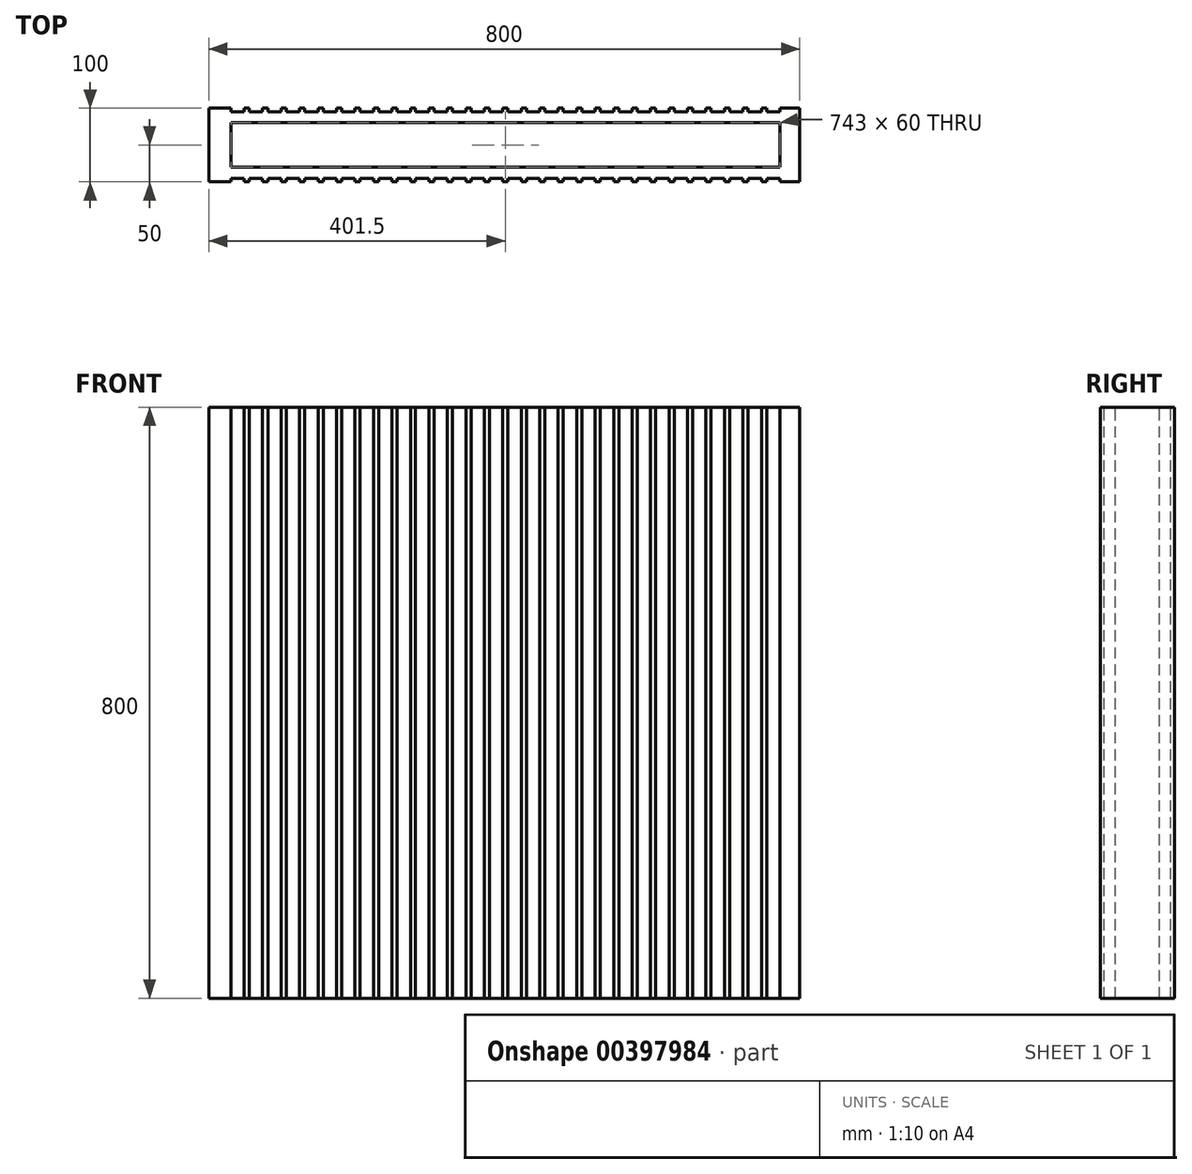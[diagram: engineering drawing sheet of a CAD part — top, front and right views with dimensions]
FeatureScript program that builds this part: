
annotation { "Feature Type Name" : "Feature", "Feature Type Description" : "" }
export const myFeature = defineFeature(function(context is Context, id is Id, definition is map)
    precondition{}
    {
        {
            var Q0;
            Q0=qCreatedBy(makeId("Top.planeOp"),FACE);
            var sketch = newSketch(context, id + "F0", { "sketchPlane" : qUnion([Q0])});
            skLineSegment(sketch, "E0.bottom", {"start": v(0, 0) * mm, "end": v(800, 0) * mm});
            skLineSegment(sketch, "E0.top", {"start": v(0, 100) * mm, "end": v(800, 100) * mm});
            skLineSegment(sketch, "E0.left", {"start": v(0, 0) * mm, "end": v(0, 100) * mm});
            skLineSegment(sketch, "E0.right", {"start": v(800, 0) * mm, "end": v(800, 100) * mm});
            skSolve(sketch);
        }
        {
            var Q0;
            Q0=makeQuery(id+"F0.imprint","IMPRINT",FACE,{"disambiguationData":[TD([[makeQuery(id+"F0.imprint","IMPRINT",EDGE,{"derivedFrom":sQuery(id+"F0.wireOp",EDGE,"E0.bottom")}),1.0]])]});
            extrude(context, id + "F1", {"entities" : qUnion([Q0]), "depth" : 800 * mm, "offsetDistance" : 25 * mm});
        }
        {
            var Q0;
            Q0=makeQuery(id+"F1.opExtrude","CAP_FACE",FACE,{"disambiguationData":[OSD([sQuery(id+"F0.wireOp",EDGE,"E0.bottom"),sQuery(id+"F0.wireOp",EDGE,"E0.top"),sQuery(id+"F0.wireOp",EDGE,"E0.left"),sQuery(id+"F0.wireOp",EDGE,"E0.right")])],"isStart":false});
            var sketch = newSketch(context, id + "F2", { "sketchPlane" : qUnion([Q0])});
            skLineSegment(sketch, "E1.top", {"start": v(30, 20) * mm, "end": v(773, 20) * mm});
            skLineSegment(sketch, "E1.left", {"start": v(30, 50) * mm, "end": v(30, 20) * mm});
            skLineSegment(sketch, "E1.right", {"start": v(773, 50) * mm, "end": v(773, 20) * mm});
            skLineSegment(sketch, "E2.bottom", {"start": v(30, 0) * mm, "end": v(48, 0) * mm});
            skLineSegment(sketch, "E2.top", {"start": v(30, 5) * mm, "end": v(48, 5) * mm});
            skLineSegment(sketch, "E2.left", {"start": v(30, 0) * mm, "end": v(30, 5) * mm});
            skLineSegment(sketch, "E2.right", {"start": v(48, 0) * mm, "end": v(48, 5) * mm});
            skLineSegment(sketch, "E3", {"start": v(0, 50) * mm, "end": v(975.65, 50) * mm, "construction": true});
            skLineSegment(sketch, "E4.1.0.0", {"start": v(55, 0) * mm, "end": v(73, 0) * mm});
            skLineSegment(sketch, "E4.1.0.1", {"start": v(55, 5) * mm, "end": v(73, 5) * mm});
            skLineSegment(sketch, "E4.1.0.2", {"start": v(73, 0) * mm, "end": v(73, 5) * mm});
            skLineSegment(sketch, "E4.1.0.3", {"start": v(55, 0) * mm, "end": v(55, 5) * mm});
            skLineSegment(sketch, "E4.2.0.0", {"start": v(80, 0) * mm, "end": v(98, 0) * mm});
            skLineSegment(sketch, "E4.2.0.1", {"start": v(80, 5) * mm, "end": v(98, 5) * mm});
            skLineSegment(sketch, "E4.2.0.2", {"start": v(98, 0) * mm, "end": v(98, 5) * mm});
            skLineSegment(sketch, "E4.2.0.3", {"start": v(80, 0) * mm, "end": v(80, 5) * mm});
            skLineSegment(sketch, "E4.3.0.0", {"start": v(105, 0) * mm, "end": v(123, 0) * mm});
            skLineSegment(sketch, "E4.3.0.1", {"start": v(105, 5) * mm, "end": v(123, 5) * mm});
            skLineSegment(sketch, "E4.3.0.2", {"start": v(123, 0) * mm, "end": v(123, 5) * mm});
            skLineSegment(sketch, "E4.3.0.3", {"start": v(105, 0) * mm, "end": v(105, 5) * mm});
            skLineSegment(sketch, "E4.4.0.0", {"start": v(130, 0) * mm, "end": v(148, 0) * mm});
            skLineSegment(sketch, "E4.4.0.1", {"start": v(130, 5) * mm, "end": v(148, 5) * mm});
            skLineSegment(sketch, "E4.4.0.2", {"start": v(148, 0) * mm, "end": v(148, 5) * mm});
            skLineSegment(sketch, "E4.4.0.3", {"start": v(130, 0) * mm, "end": v(130, 5) * mm});
            skLineSegment(sketch, "E4.5.0.0", {"start": v(155, 0) * mm, "end": v(173, 0) * mm});
            skLineSegment(sketch, "E4.5.0.1", {"start": v(155, 5) * mm, "end": v(173, 5) * mm});
            skLineSegment(sketch, "E4.5.0.2", {"start": v(173, 0) * mm, "end": v(173, 5) * mm});
            skLineSegment(sketch, "E4.5.0.3", {"start": v(155, 0) * mm, "end": v(155, 5) * mm});
            skLineSegment(sketch, "E4.6.0.0", {"start": v(180, 0) * mm, "end": v(198, 0) * mm});
            skLineSegment(sketch, "E4.6.0.1", {"start": v(180, 5) * mm, "end": v(198, 5) * mm});
            skLineSegment(sketch, "E4.6.0.2", {"start": v(198, 0) * mm, "end": v(198, 5) * mm});
            skLineSegment(sketch, "E4.6.0.3", {"start": v(180, 0) * mm, "end": v(180, 5) * mm});
            skLineSegment(sketch, "E4.7.0.0", {"start": v(205, 0) * mm, "end": v(223, 0) * mm});
            skLineSegment(sketch, "E4.7.0.1", {"start": v(205, 5) * mm, "end": v(223, 5) * mm});
            skLineSegment(sketch, "E4.7.0.2", {"start": v(223, 0) * mm, "end": v(223, 5) * mm});
            skLineSegment(sketch, "E4.7.0.3", {"start": v(205, 0) * mm, "end": v(205, 5) * mm});
            skLineSegment(sketch, "E4.8.0.0", {"start": v(230, 0) * mm, "end": v(248, 0) * mm});
            skLineSegment(sketch, "E4.8.0.1", {"start": v(230, 5) * mm, "end": v(248, 5) * mm});
            skLineSegment(sketch, "E4.8.0.2", {"start": v(248, 0) * mm, "end": v(248, 5) * mm});
            skLineSegment(sketch, "E4.8.0.3", {"start": v(230, 0) * mm, "end": v(230, 5) * mm});
            skLineSegment(sketch, "E4.9.0.0", {"start": v(255, 0) * mm, "end": v(273, 0) * mm});
            skLineSegment(sketch, "E4.9.0.1", {"start": v(255, 5) * mm, "end": v(273, 5) * mm});
            skLineSegment(sketch, "E4.9.0.2", {"start": v(273, 0) * mm, "end": v(273, 5) * mm});
            skLineSegment(sketch, "E4.9.0.3", {"start": v(255, 0) * mm, "end": v(255, 5) * mm});
            skLineSegment(sketch, "E4.10.0.0", {"start": v(280, 0) * mm, "end": v(298, 0) * mm});
            skLineSegment(sketch, "E4.10.0.1", {"start": v(280, 5) * mm, "end": v(298, 5) * mm});
            skLineSegment(sketch, "E4.10.0.2", {"start": v(298, 0) * mm, "end": v(298, 5) * mm});
            skLineSegment(sketch, "E4.10.0.3", {"start": v(280, 0) * mm, "end": v(280, 5) * mm});
            skLineSegment(sketch, "E4.11.0.0", {"start": v(305, 0) * mm, "end": v(323, 0) * mm});
            skLineSegment(sketch, "E4.11.0.1", {"start": v(305, 5) * mm, "end": v(323, 5) * mm});
            skLineSegment(sketch, "E4.11.0.2", {"start": v(323, 0) * mm, "end": v(323, 5) * mm});
            skLineSegment(sketch, "E4.11.0.3", {"start": v(305, 0) * mm, "end": v(305, 5) * mm});
            skLineSegment(sketch, "E4.12.0.0", {"start": v(330, 0) * mm, "end": v(348, 0) * mm});
            skLineSegment(sketch, "E4.12.0.1", {"start": v(330, 5) * mm, "end": v(348, 5) * mm});
            skLineSegment(sketch, "E4.12.0.2", {"start": v(348, 0) * mm, "end": v(348, 5) * mm});
            skLineSegment(sketch, "E4.12.0.3", {"start": v(330, 0) * mm, "end": v(330, 5) * mm});
            skLineSegment(sketch, "E4.13.0.0", {"start": v(355, 0) * mm, "end": v(373, 0) * mm});
            skLineSegment(sketch, "E4.13.0.1", {"start": v(355, 5) * mm, "end": v(373, 5) * mm});
            skLineSegment(sketch, "E4.13.0.2", {"start": v(373, 0) * mm, "end": v(373, 5) * mm});
            skLineSegment(sketch, "E4.13.0.3", {"start": v(355, 0) * mm, "end": v(355, 5) * mm});
            skLineSegment(sketch, "E4.14.0.0", {"start": v(380, 0) * mm, "end": v(398, 0) * mm});
            skLineSegment(sketch, "E4.14.0.1", {"start": v(380, 5) * mm, "end": v(398, 5) * mm});
            skLineSegment(sketch, "E4.14.0.2", {"start": v(398, 0) * mm, "end": v(398, 5) * mm});
            skLineSegment(sketch, "E4.14.0.3", {"start": v(380, 0) * mm, "end": v(380, 5) * mm});
            skLineSegment(sketch, "E4.15.0.0", {"start": v(405, 0) * mm, "end": v(423, 0) * mm});
            skLineSegment(sketch, "E4.15.0.1", {"start": v(405, 5) * mm, "end": v(423, 5) * mm});
            skLineSegment(sketch, "E4.15.0.2", {"start": v(423, 0) * mm, "end": v(423, 5) * mm});
            skLineSegment(sketch, "E4.15.0.3", {"start": v(405, 0) * mm, "end": v(405, 5) * mm});
            skLineSegment(sketch, "E4.16.0.0", {"start": v(430, 0) * mm, "end": v(448, 0) * mm});
            skLineSegment(sketch, "E4.16.0.1", {"start": v(430, 5) * mm, "end": v(448, 5) * mm});
            skLineSegment(sketch, "E4.16.0.2", {"start": v(448, 0) * mm, "end": v(448, 5) * mm});
            skLineSegment(sketch, "E4.16.0.3", {"start": v(430, 0) * mm, "end": v(430, 5) * mm});
            skLineSegment(sketch, "E4.17.0.0", {"start": v(455, 0) * mm, "end": v(473, 0) * mm});
            skLineSegment(sketch, "E4.17.0.1", {"start": v(455, 5) * mm, "end": v(473, 5) * mm});
            skLineSegment(sketch, "E4.17.0.2", {"start": v(473, 0) * mm, "end": v(473, 5) * mm});
            skLineSegment(sketch, "E4.17.0.3", {"start": v(455, 0) * mm, "end": v(455, 5) * mm});
            skLineSegment(sketch, "E4.18.0.0", {"start": v(480, 0) * mm, "end": v(498, 0) * mm});
            skLineSegment(sketch, "E4.18.0.1", {"start": v(480, 5) * mm, "end": v(498, 5) * mm});
            skLineSegment(sketch, "E4.18.0.2", {"start": v(498, 0) * mm, "end": v(498, 5) * mm});
            skLineSegment(sketch, "E4.18.0.3", {"start": v(480, 0) * mm, "end": v(480, 5) * mm});
            skLineSegment(sketch, "E4.19.0.0", {"start": v(505, 0) * mm, "end": v(523, 0) * mm});
            skLineSegment(sketch, "E4.19.0.1", {"start": v(505, 5) * mm, "end": v(523, 5) * mm});
            skLineSegment(sketch, "E4.19.0.2", {"start": v(523, 0) * mm, "end": v(523, 5) * mm});
            skLineSegment(sketch, "E4.19.0.3", {"start": v(505, 0) * mm, "end": v(505, 5) * mm});
            skLineSegment(sketch, "E4.20.0.0", {"start": v(530, 0) * mm, "end": v(548, 0) * mm});
            skLineSegment(sketch, "E4.20.0.1", {"start": v(530, 5) * mm, "end": v(548, 5) * mm});
            skLineSegment(sketch, "E4.20.0.2", {"start": v(548, 0) * mm, "end": v(548, 5) * mm});
            skLineSegment(sketch, "E4.20.0.3", {"start": v(530, 0) * mm, "end": v(530, 5) * mm});
            skLineSegment(sketch, "E4.21.0.0", {"start": v(555, 0) * mm, "end": v(573, 0) * mm});
            skLineSegment(sketch, "E4.21.0.1", {"start": v(555, 5) * mm, "end": v(573, 5) * mm});
            skLineSegment(sketch, "E4.21.0.2", {"start": v(573, 0) * mm, "end": v(573, 5) * mm});
            skLineSegment(sketch, "E4.21.0.3", {"start": v(555, 0) * mm, "end": v(555, 5) * mm});
            skLineSegment(sketch, "E4.22.0.0", {"start": v(580, 0) * mm, "end": v(598, 0) * mm});
            skLineSegment(sketch, "E4.22.0.1", {"start": v(580, 5) * mm, "end": v(598, 5) * mm});
            skLineSegment(sketch, "E4.22.0.2", {"start": v(598, 0) * mm, "end": v(598, 5) * mm});
            skLineSegment(sketch, "E4.22.0.3", {"start": v(580, 0) * mm, "end": v(580, 5) * mm});
            skLineSegment(sketch, "E4.23.0.0", {"start": v(605, 0) * mm, "end": v(623, 0) * mm});
            skLineSegment(sketch, "E4.23.0.1", {"start": v(605, 5) * mm, "end": v(623, 5) * mm});
            skLineSegment(sketch, "E4.23.0.2", {"start": v(623, 0) * mm, "end": v(623, 5) * mm});
            skLineSegment(sketch, "E4.23.0.3", {"start": v(605, 0) * mm, "end": v(605, 5) * mm});
            skLineSegment(sketch, "E4.24.0.0", {"start": v(630, 0) * mm, "end": v(648, 0) * mm});
            skLineSegment(sketch, "E4.24.0.1", {"start": v(630, 5) * mm, "end": v(648, 5) * mm});
            skLineSegment(sketch, "E4.24.0.2", {"start": v(648, 0) * mm, "end": v(648, 5) * mm});
            skLineSegment(sketch, "E4.24.0.3", {"start": v(630, 0) * mm, "end": v(630, 5) * mm});
            skLineSegment(sketch, "E4.25.0.0", {"start": v(655, 0) * mm, "end": v(673, 0) * mm});
            skLineSegment(sketch, "E4.25.0.1", {"start": v(655, 5) * mm, "end": v(673, 5) * mm});
            skLineSegment(sketch, "E4.25.0.2", {"start": v(673, 0) * mm, "end": v(673, 5) * mm});
            skLineSegment(sketch, "E4.25.0.3", {"start": v(655, 0) * mm, "end": v(655, 5) * mm});
            skLineSegment(sketch, "E4.26.0.0", {"start": v(680, 0) * mm, "end": v(698, 0) * mm});
            skLineSegment(sketch, "E4.26.0.1", {"start": v(680, 5) * mm, "end": v(698, 5) * mm});
            skLineSegment(sketch, "E4.26.0.2", {"start": v(698, 0) * mm, "end": v(698, 5) * mm});
            skLineSegment(sketch, "E4.26.0.3", {"start": v(680, 0) * mm, "end": v(680, 5) * mm});
            skLineSegment(sketch, "E4.27.0.0", {"start": v(705, 0) * mm, "end": v(723, 0) * mm});
            skLineSegment(sketch, "E4.27.0.1", {"start": v(705, 5) * mm, "end": v(723, 5) * mm});
            skLineSegment(sketch, "E4.27.0.2", {"start": v(723, 0) * mm, "end": v(723, 5) * mm});
            skLineSegment(sketch, "E4.27.0.3", {"start": v(705, 0) * mm, "end": v(705, 5) * mm});
            skLineSegment(sketch, "E4.28.0.0", {"start": v(730, 0) * mm, "end": v(748, 0) * mm});
            skLineSegment(sketch, "E4.28.0.1", {"start": v(730, 5) * mm, "end": v(748, 5) * mm});
            skLineSegment(sketch, "E4.28.0.2", {"start": v(748, 0) * mm, "end": v(748, 5) * mm});
            skLineSegment(sketch, "E4.28.0.3", {"start": v(730, 0) * mm, "end": v(730, 5) * mm});
            skLineSegment(sketch, "E4.29.0.0", {"start": v(755, 0) * mm, "end": v(773, 0) * mm});
            skLineSegment(sketch, "E4.29.0.1", {"start": v(755, 5) * mm, "end": v(773, 5) * mm});
            skLineSegment(sketch, "E4.29.0.2", {"start": v(773, 0) * mm, "end": v(773, 5) * mm});
            skLineSegment(sketch, "E4.29.0.3", {"start": v(755, 0) * mm, "end": v(755, 5) * mm});
            skLineSegment(sketch, "E4.direction1", {"start": v(30, 0) * mm, "end": v(55, 0) * mm, "construction": true});
            skLineSegment(sketch, "E5.MirrorCS", {"start": v(673, 100) * mm, "end": v(673, 95) * mm});
            skLineSegment(sketch, "E6.MirrorCS", {"start": v(355, 100) * mm, "end": v(355, 95) * mm});
            skLineSegment(sketch, "E7.MirrorCS", {"start": v(255, 100) * mm, "end": v(255, 95) * mm});
            skLineSegment(sketch, "E8.MirrorCS", {"start": v(198, 100) * mm, "end": v(198, 95) * mm});
            skLineSegment(sketch, "E9.MirrorCS", {"start": v(680, 100) * mm, "end": v(680, 95) * mm});
            skLineSegment(sketch, "E10.MirrorCS", {"start": v(205, 100) * mm, "end": v(205, 95) * mm});
            skLineSegment(sketch, "E11.MirrorCS", {"start": v(348, 100) * mm, "end": v(348, 95) * mm});
            skLineSegment(sketch, "E12.MirrorCS", {"start": v(248, 100) * mm, "end": v(248, 95) * mm});
            skLineSegment(sketch, "E13.MirrorCS", {"start": v(30, 100) * mm, "end": v(48, 100) * mm});
            skLineSegment(sketch, "E14.MirrorCS", {"start": v(373, 100) * mm, "end": v(373, 95) * mm});
            skLineSegment(sketch, "E15.MirrorCS", {"start": v(273, 100) * mm, "end": v(273, 95) * mm});
            skLineSegment(sketch, "E16.MirrorCS", {"start": v(173, 100) * mm, "end": v(173, 95) * mm});
            skLineSegment(sketch, "E17.MirrorCS", {"start": v(573, 100) * mm, "end": v(573, 95) * mm});
            skLineSegment(sketch, "E18.MirrorCS", {"start": v(30, 100) * mm, "end": v(55, 100) * mm, "construction": true});
            skLineSegment(sketch, "E19.MirrorCS", {"start": v(455, 100) * mm, "end": v(455, 95) * mm});
            skLineSegment(sketch, "E20.MirrorCS", {"start": v(755, 100) * mm, "end": v(755, 95) * mm});
            skLineSegment(sketch, "E21.MirrorCS", {"start": v(655, 100) * mm, "end": v(655, 95) * mm});
            skLineSegment(sketch, "E22.MirrorCS", {"start": v(80, 100) * mm, "end": v(80, 95) * mm});
            skLineSegment(sketch, "E23.MirrorCS", {"start": v(30, 95) * mm, "end": v(48, 95) * mm});
            skLineSegment(sketch, "E24.MirrorCS", {"start": v(30, 100) * mm, "end": v(30, 95) * mm});
            skLineSegment(sketch, "E25.MirrorCS", {"start": v(48, 100) * mm, "end": v(48, 95) * mm});
            skLineSegment(sketch, "E26.MirrorCS", {"start": v(55, 100) * mm, "end": v(73, 100) * mm});
            skLineSegment(sketch, "E27.MirrorCS", {"start": v(55, 95) * mm, "end": v(73, 95) * mm});
            skLineSegment(sketch, "E28.MirrorCS", {"start": v(73, 100) * mm, "end": v(73, 95) * mm});
            skLineSegment(sketch, "E29.MirrorCS", {"start": v(55, 100) * mm, "end": v(55, 95) * mm});
            skLineSegment(sketch, "E30.MirrorCS", {"start": v(473, 100) * mm, "end": v(473, 95) * mm});
            skLineSegment(sketch, "E31.MirrorCS", {"start": v(773, 100) * mm, "end": v(773, 95) * mm});
            skLineSegment(sketch, "E32.MirrorCS", {"start": v(180, 100) * mm, "end": v(198, 100) * mm});
            skLineSegment(sketch, "E33.MirrorCS", {"start": v(580, 100) * mm, "end": v(598, 100) * mm});
            skLineSegment(sketch, "E34.MirrorCS", {"start": v(480, 100) * mm, "end": v(498, 100) * mm});
            skLineSegment(sketch, "E35.MirrorCS", {"start": v(380, 100) * mm, "end": v(398, 100) * mm});
            skLineSegment(sketch, "E36.MirrorCS", {"start": v(280, 100) * mm, "end": v(298, 100) * mm});
            skLineSegment(sketch, "E37.MirrorCS", {"start": v(680, 100) * mm, "end": v(698, 100) * mm});
            skLineSegment(sketch, "E38.MirrorCS", {"start": v(155, 100) * mm, "end": v(155, 95) * mm});
            skLineSegment(sketch, "E39.MirrorCS", {"start": v(555, 100) * mm, "end": v(555, 95) * mm});
            skLineSegment(sketch, "E40.MirrorCS", {"start": v(180, 95) * mm, "end": v(198, 95) * mm});
            skLineSegment(sketch, "E41.MirrorCS", {"start": v(580, 95) * mm, "end": v(598, 95) * mm});
            skLineSegment(sketch, "E42.MirrorCS", {"start": v(480, 95) * mm, "end": v(498, 95) * mm});
            skLineSegment(sketch, "E43.MirrorCS", {"start": v(380, 95) * mm, "end": v(398, 95) * mm});
            skLineSegment(sketch, "E44.MirrorCS", {"start": v(280, 95) * mm, "end": v(298, 95) * mm});
            skLineSegment(sketch, "E45.MirrorCS", {"start": v(680, 95) * mm, "end": v(698, 95) * mm});
            skLineSegment(sketch, "E46.MirrorCS", {"start": v(598, 100) * mm, "end": v(598, 95) * mm});
            skLineSegment(sketch, "E47.MirrorCS", {"start": v(498, 100) * mm, "end": v(498, 95) * mm});
            skLineSegment(sketch, "E48.MirrorCS", {"start": v(398, 100) * mm, "end": v(398, 95) * mm});
            skLineSegment(sketch, "E49.MirrorCS", {"start": v(298, 100) * mm, "end": v(298, 95) * mm});
            skLineSegment(sketch, "E50.MirrorCS", {"start": v(698, 100) * mm, "end": v(698, 95) * mm});
            skLineSegment(sketch, "E51.MirrorCS", {"start": v(580, 100) * mm, "end": v(580, 95) * mm});
            skLineSegment(sketch, "E52.MirrorCS", {"start": v(480, 100) * mm, "end": v(480, 95) * mm});
            skLineSegment(sketch, "E53.MirrorCS", {"start": v(380, 100) * mm, "end": v(380, 95) * mm});
            skLineSegment(sketch, "E54.MirrorCS", {"start": v(280, 100) * mm, "end": v(280, 95) * mm});
            skLineSegment(sketch, "E55.MirrorCS", {"start": v(180, 100) * mm, "end": v(180, 95) * mm});
            skLineSegment(sketch, "E56.MirrorCS", {"start": v(705, 100) * mm, "end": v(723, 100) * mm});
            skLineSegment(sketch, "E57.MirrorCS", {"start": v(205, 100) * mm, "end": v(223, 100) * mm});
            skLineSegment(sketch, "E58.MirrorCS", {"start": v(105, 100) * mm, "end": v(123, 100) * mm});
            skLineSegment(sketch, "E59.MirrorCS", {"start": v(605, 100) * mm, "end": v(623, 100) * mm});
            skLineSegment(sketch, "E60.MirrorCS", {"start": v(505, 100) * mm, "end": v(523, 100) * mm});
            skLineSegment(sketch, "E61.MirrorCS", {"start": v(405, 100) * mm, "end": v(423, 100) * mm});
            skLineSegment(sketch, "E62.MirrorCS", {"start": v(305, 100) * mm, "end": v(323, 100) * mm});
            skLineSegment(sketch, "E63.MirrorCS", {"start": v(205, 95) * mm, "end": v(223, 95) * mm});
            skLineSegment(sketch, "E64.MirrorCS", {"start": v(105, 95) * mm, "end": v(123, 95) * mm});
            skLineSegment(sketch, "E65.MirrorCS", {"start": v(605, 95) * mm, "end": v(623, 95) * mm});
            skLineSegment(sketch, "E66.MirrorCS", {"start": v(505, 95) * mm, "end": v(523, 95) * mm});
            skLineSegment(sketch, "E67.MirrorCS", {"start": v(405, 95) * mm, "end": v(423, 95) * mm});
            skLineSegment(sketch, "E68.MirrorCS", {"start": v(305, 95) * mm, "end": v(323, 95) * mm});
            skLineSegment(sketch, "E69.MirrorCS", {"start": v(705, 95) * mm, "end": v(723, 95) * mm});
            skLineSegment(sketch, "E70.MirrorCS", {"start": v(223, 100) * mm, "end": v(223, 95) * mm});
            skLineSegment(sketch, "E71.MirrorCS", {"start": v(123, 100) * mm, "end": v(123, 95) * mm});
            skLineSegment(sketch, "E72.MirrorCS", {"start": v(623, 100) * mm, "end": v(623, 95) * mm});
            skLineSegment(sketch, "E73.MirrorCS", {"start": v(523, 100) * mm, "end": v(523, 95) * mm});
            skLineSegment(sketch, "E74.MirrorCS", {"start": v(423, 100) * mm, "end": v(423, 95) * mm});
            skLineSegment(sketch, "E75.MirrorCS", {"start": v(323, 100) * mm, "end": v(323, 95) * mm});
            skLineSegment(sketch, "E76.MirrorCS", {"start": v(723, 100) * mm, "end": v(723, 95) * mm});
            skLineSegment(sketch, "E77.MirrorCS", {"start": v(105, 100) * mm, "end": v(105, 95) * mm});
            skLineSegment(sketch, "E78.MirrorCS", {"start": v(605, 100) * mm, "end": v(605, 95) * mm});
            skLineSegment(sketch, "E79.MirrorCS", {"start": v(505, 100) * mm, "end": v(505, 95) * mm});
            skLineSegment(sketch, "E80.MirrorCS", {"start": v(405, 100) * mm, "end": v(405, 95) * mm});
            skLineSegment(sketch, "E81.MirrorCS", {"start": v(305, 100) * mm, "end": v(305, 95) * mm});
            skLineSegment(sketch, "E82.MirrorCS", {"start": v(705, 100) * mm, "end": v(705, 95) * mm});
            skLineSegment(sketch, "E83.MirrorCS", {"start": v(230, 100) * mm, "end": v(248, 100) * mm});
            skLineSegment(sketch, "E84.MirrorCS", {"start": v(130, 100) * mm, "end": v(148, 100) * mm});
            skLineSegment(sketch, "E85.MirrorCS", {"start": v(630, 100) * mm, "end": v(648, 100) * mm});
            skLineSegment(sketch, "E86.MirrorCS", {"start": v(530, 100) * mm, "end": v(548, 100) * mm});
            skLineSegment(sketch, "E87.MirrorCS", {"start": v(430, 100) * mm, "end": v(448, 100) * mm});
            skLineSegment(sketch, "E88.MirrorCS", {"start": v(330, 100) * mm, "end": v(348, 100) * mm});
            skLineSegment(sketch, "E89.MirrorCS", {"start": v(730, 100) * mm, "end": v(748, 100) * mm});
            skLineSegment(sketch, "E90.MirrorCS", {"start": v(230, 95) * mm, "end": v(248, 95) * mm});
            skLineSegment(sketch, "E91.MirrorCS", {"start": v(130, 95) * mm, "end": v(148, 95) * mm});
            skLineSegment(sketch, "E92.MirrorCS", {"start": v(630, 95) * mm, "end": v(648, 95) * mm});
            skLineSegment(sketch, "E93.MirrorCS", {"start": v(530, 95) * mm, "end": v(548, 95) * mm});
            skLineSegment(sketch, "E94.MirrorCS", {"start": v(430, 95) * mm, "end": v(448, 95) * mm});
            skLineSegment(sketch, "E95.MirrorCS", {"start": v(330, 95) * mm, "end": v(348, 95) * mm});
            skLineSegment(sketch, "E96.MirrorCS", {"start": v(730, 95) * mm, "end": v(748, 95) * mm});
            skLineSegment(sketch, "E97.MirrorCS", {"start": v(448, 100) * mm, "end": v(448, 95) * mm});
            skLineSegment(sketch, "E98.MirrorCS", {"start": v(148, 100) * mm, "end": v(148, 95) * mm});
            skLineSegment(sketch, "E99.MirrorCS", {"start": v(748, 100) * mm, "end": v(748, 95) * mm});
            skLineSegment(sketch, "E100.MirrorCS", {"start": v(648, 100) * mm, "end": v(648, 95) * mm});
            skLineSegment(sketch, "E101.MirrorCS", {"start": v(548, 100) * mm, "end": v(548, 95) * mm});
            skLineSegment(sketch, "E102.MirrorCS", {"start": v(430, 100) * mm, "end": v(430, 95) * mm});
            skLineSegment(sketch, "E103.MirrorCS", {"start": v(330, 100) * mm, "end": v(330, 95) * mm});
            skLineSegment(sketch, "E104.MirrorCS", {"start": v(230, 100) * mm, "end": v(230, 95) * mm});
            skLineSegment(sketch, "E105.MirrorCS", {"start": v(130, 100) * mm, "end": v(130, 95) * mm});
            skLineSegment(sketch, "E106.MirrorCS", {"start": v(730, 100) * mm, "end": v(730, 95) * mm});
            skLineSegment(sketch, "E107.MirrorCS", {"start": v(630, 100) * mm, "end": v(630, 95) * mm});
            skLineSegment(sketch, "E108.MirrorCS", {"start": v(530, 100) * mm, "end": v(530, 95) * mm});
            skLineSegment(sketch, "E109.MirrorCS", {"start": v(80, 100) * mm, "end": v(98, 100) * mm});
            skLineSegment(sketch, "E110.MirrorCS", {"start": v(80, 95) * mm, "end": v(98, 95) * mm});
            skLineSegment(sketch, "E111.MirrorCS", {"start": v(98, 100) * mm, "end": v(98, 95) * mm});
            skLineSegment(sketch, "E112.MirrorCS", {"start": v(455, 100) * mm, "end": v(473, 100) * mm});
            skLineSegment(sketch, "E113.MirrorCS", {"start": v(355, 100) * mm, "end": v(373, 100) * mm});
            skLineSegment(sketch, "E114.MirrorCS", {"start": v(255, 100) * mm, "end": v(273, 100) * mm});
            skLineSegment(sketch, "E115.MirrorCS", {"start": v(155, 100) * mm, "end": v(173, 100) * mm});
            skLineSegment(sketch, "E116.MirrorCS", {"start": v(755, 100) * mm, "end": v(773, 100) * mm});
            skLineSegment(sketch, "E117.MirrorCS", {"start": v(655, 100) * mm, "end": v(673, 100) * mm});
            skLineSegment(sketch, "E118.MirrorCS", {"start": v(555, 100) * mm, "end": v(573, 100) * mm});
            skLineSegment(sketch, "E119.MirrorCS", {"start": v(455, 95) * mm, "end": v(473, 95) * mm});
            skLineSegment(sketch, "E120.MirrorCS", {"start": v(355, 95) * mm, "end": v(373, 95) * mm});
            skLineSegment(sketch, "E121.MirrorCS", {"start": v(255, 95) * mm, "end": v(273, 95) * mm});
            skLineSegment(sketch, "E122.MirrorCS", {"start": v(155, 95) * mm, "end": v(173, 95) * mm});
            skLineSegment(sketch, "E123.MirrorCS", {"start": v(755, 95) * mm, "end": v(773, 95) * mm});
            skLineSegment(sketch, "E124.MirrorCS", {"start": v(655, 95) * mm, "end": v(673, 95) * mm});
            skLineSegment(sketch, "E125.MirrorCS", {"start": v(555, 95) * mm, "end": v(573, 95) * mm});
            skLineSegment(sketch, "E126.MirrorCS", {"start": v(773, 50) * mm, "end": v(773, 80) * mm});
            skLineSegment(sketch, "E127.MirrorCS", {"start": v(30, 80) * mm, "end": v(773, 80) * mm});
            skLineSegment(sketch, "E128.MirrorCS", {"start": v(30, 50) * mm, "end": v(30, 80) * mm});
            skSolve(sketch);
        }
        {
            var Q0;
            Q0=makeQuery(id+"F2.imprint","IMPRINT",FACE,{"disambiguationData":[TD([[makeQuery(id+"F2.imprint","IMPRINT",EDGE,{"derivedFrom":sQuery(id+"F2.wireOp",EDGE,"E1.top")}),1.0]])]});
            var Q1;
            Q1=makeQuery(id+"F2.imprint","IMPRINT",FACE,{"disambiguationData":[TD([[makeQuery(id+"F2.imprint","IMPRINT",EDGE,{"derivedFrom":sQuery(id+"F2.wireOp",EDGE,"E2.bottom")}),1.0]])]});
            var Q2;
            Q2=makeQuery(id+"F2.imprint","IMPRINT",FACE,{"disambiguationData":[TD([[makeQuery(id+"F2.imprint","IMPRINT",EDGE,{"derivedFrom":sQuery(id+"F2.wireOp",EDGE,"E4.1.0.0")}),1.0]])]});
            var Q3;
            Q3=makeQuery(id+"F2.imprint","IMPRINT",FACE,{"disambiguationData":[TD([[makeQuery(id+"F2.imprint","IMPRINT",EDGE,{"derivedFrom":sQuery(id+"F2.wireOp",EDGE,"E4.2.0.0")}),1.0]])]});
            var Q4;
            Q4=makeQuery(id+"F2.imprint","IMPRINT",FACE,{"disambiguationData":[TD([[makeQuery(id+"F2.imprint","IMPRINT",EDGE,{"derivedFrom":sQuery(id+"F2.wireOp",EDGE,"E4.3.0.0")}),1.0]])]});
            var Q5;
            Q5=makeQuery(id+"F2.imprint","IMPRINT",FACE,{"disambiguationData":[TD([[makeQuery(id+"F2.imprint","IMPRINT",EDGE,{"derivedFrom":sQuery(id+"F2.wireOp",EDGE,"E4.4.0.0")}),1.0]])]});
            var Q6;
            Q6=makeQuery(id+"F2.imprint","IMPRINT",FACE,{"disambiguationData":[TD([[makeQuery(id+"F2.imprint","IMPRINT",EDGE,{"derivedFrom":sQuery(id+"F2.wireOp",EDGE,"E11.MirrorCS")}),-1.0]])]});
            var Q7;
            Q7=makeQuery(id+"F2.imprint","IMPRINT",FACE,{"disambiguationData":[TD([[makeQuery(id+"F2.imprint","IMPRINT",EDGE,{"derivedFrom":sQuery(id+"F2.wireOp",EDGE,"E4.10.0.0")}),1.0]])]});
            var Q8;
            Q8=makeQuery(id+"F2.imprint","IMPRINT",FACE,{"disambiguationData":[TD([[makeQuery(id+"F2.imprint","IMPRINT",EDGE,{"derivedFrom":sQuery(id+"F2.wireOp",EDGE,"E4.9.0.0")}),1.0]])]});
            var Q9;
            Q9=makeQuery(id+"F2.imprint","IMPRINT",FACE,{"disambiguationData":[TD([[makeQuery(id+"F2.imprint","IMPRINT",EDGE,{"derivedFrom":sQuery(id+"F2.wireOp",EDGE,"E4.8.0.0")}),1.0]])]});
            var Q10;
            Q10=makeQuery(id+"F2.imprint","IMPRINT",FACE,{"disambiguationData":[TD([[makeQuery(id+"F2.imprint","IMPRINT",EDGE,{"derivedFrom":sQuery(id+"F2.wireOp",EDGE,"E9.MirrorCS")}),1.0]])]});
            var Q11;
            Q11=makeQuery(id+"F2.imprint","IMPRINT",FACE,{"disambiguationData":[TD([[makeQuery(id+"F2.imprint","IMPRINT",EDGE,{"derivedFrom":sQuery(id+"F2.wireOp",EDGE,"E6.MirrorCS")}),1.0]])]});
            var Q12;
            Q12=makeQuery(id+"F2.imprint","IMPRINT",FACE,{"disambiguationData":[TD([[makeQuery(id+"F2.imprint","IMPRINT",EDGE,{"derivedFrom":sQuery(id+"F2.wireOp",EDGE,"E4.24.0.0")}),1.0]])]});
            var Q13;
            Q13=makeQuery(id+"F2.imprint","IMPRINT",FACE,{"disambiguationData":[TD([[makeQuery(id+"F2.imprint","IMPRINT",EDGE,{"derivedFrom":sQuery(id+"F2.wireOp",EDGE,"E4.23.0.0")}),1.0]])]});
            var Q14;
            Q14=makeQuery(id+"F2.imprint","IMPRINT",FACE,{"disambiguationData":[TD([[makeQuery(id+"F2.imprint","IMPRINT",EDGE,{"derivedFrom":sQuery(id+"F2.wireOp",EDGE,"E4.22.0.0")}),1.0]])]});
            var Q15;
            Q15=makeQuery(id+"F2.imprint","IMPRINT",FACE,{"disambiguationData":[TD([[makeQuery(id+"F2.imprint","IMPRINT",EDGE,{"derivedFrom":sQuery(id+"F2.wireOp",EDGE,"E62.MirrorCS")}),-1.0]])]});
            var Q16;
            Q16=makeQuery(id+"F2.imprint","IMPRINT",FACE,{"disambiguationData":[TD([[makeQuery(id+"F2.imprint","IMPRINT",EDGE,{"derivedFrom":sQuery(id+"F2.wireOp",EDGE,"E5.MirrorCS")}),-1.0]])]});
            var Q17;
            Q17=makeQuery(id+"F2.imprint","IMPRINT",FACE,{"disambiguationData":[TD([[makeQuery(id+"F2.imprint","IMPRINT",EDGE,{"derivedFrom":sQuery(id+"F2.wireOp",EDGE,"E4.20.0.0")}),1.0]])]});
            var Q18;
            Q18=makeQuery(id+"F2.imprint","IMPRINT",FACE,{"disambiguationData":[TD([[makeQuery(id+"F2.imprint","IMPRINT",EDGE,{"derivedFrom":sQuery(id+"F2.wireOp",EDGE,"E60.MirrorCS")}),-1.0]])]});
            var Q19;
            Q19=makeQuery(id+"F2.imprint","IMPRINT",FACE,{"disambiguationData":[TD([[makeQuery(id+"F2.imprint","IMPRINT",EDGE,{"derivedFrom":sQuery(id+"F2.wireOp",EDGE,"E4.11.0.0")}),1.0]])]});
            var Q20;
            Q20=makeQuery(id+"F2.imprint","IMPRINT",FACE,{"disambiguationData":[TD([[makeQuery(id+"F2.imprint","IMPRINT",EDGE,{"derivedFrom":sQuery(id+"F2.wireOp",EDGE,"E4.7.0.0")}),1.0]])]});
            var Q21;
            Q21=makeQuery(id+"F2.imprint","IMPRINT",FACE,{"disambiguationData":[TD([[makeQuery(id+"F2.imprint","IMPRINT",EDGE,{"derivedFrom":sQuery(id+"F2.wireOp",EDGE,"E4.6.0.0")}),1.0]])]});
            var Q22;
            Q22=makeQuery(id+"F2.imprint","IMPRINT",FACE,{"disambiguationData":[TD([[makeQuery(id+"F2.imprint","IMPRINT",EDGE,{"derivedFrom":sQuery(id+"F2.wireOp",EDGE,"E4.5.0.0")}),1.0]])]});
            var Q23;
            Q23=makeQuery(id+"F2.imprint","IMPRINT",FACE,{"disambiguationData":[TD([[makeQuery(id+"F2.imprint","IMPRINT",EDGE,{"derivedFrom":sQuery(id+"F2.wireOp",EDGE,"E4.13.0.0")}),1.0]])]});
            var Q24;
            Q24=makeQuery(id+"F2.imprint","IMPRINT",FACE,{"disambiguationData":[TD([[makeQuery(id+"F2.imprint","IMPRINT",EDGE,{"derivedFrom":sQuery(id+"F2.wireOp",EDGE,"E4.12.0.0")}),1.0]])]});
            var Q25;
            Q25=makeQuery(id+"F2.imprint","IMPRINT",FACE,{"disambiguationData":[TD([[makeQuery(id+"F2.imprint","IMPRINT",EDGE,{"derivedFrom":sQuery(id+"F2.wireOp",EDGE,"E4.14.0.0")}),1.0]])]});
            var Q26;
            Q26=makeQuery(id+"F2.imprint","IMPRINT",FACE,{"disambiguationData":[TD([[makeQuery(id+"F2.imprint","IMPRINT",EDGE,{"derivedFrom":sQuery(id+"F2.wireOp",EDGE,"E4.27.0.0")}),1.0]])]});
            var Q27;
            Q27=makeQuery(id+"F2.imprint","IMPRINT",FACE,{"disambiguationData":[TD([[makeQuery(id+"F2.imprint","IMPRINT",EDGE,{"derivedFrom":sQuery(id+"F2.wireOp",EDGE,"E59.MirrorCS")}),-1.0]])]});
            var Q28;
            Q28=makeQuery(id+"F2.imprint","IMPRINT",FACE,{"disambiguationData":[TD([[makeQuery(id+"F2.imprint","IMPRINT",EDGE,{"derivedFrom":sQuery(id+"F2.wireOp",EDGE,"E4.19.0.0")}),1.0]])]});
            var Q29;
            Q29=makeQuery(id+"F2.imprint","IMPRINT",FACE,{"disambiguationData":[TD([[makeQuery(id+"F2.imprint","IMPRINT",EDGE,{"derivedFrom":sQuery(id+"F2.wireOp",EDGE,"E10.MirrorCS")}),1.0]])]});
            var Q30;
            Q30=makeQuery(id+"F2.imprint","IMPRINT",FACE,{"disambiguationData":[TD([[makeQuery(id+"F2.imprint","IMPRINT",EDGE,{"derivedFrom":sQuery(id+"F2.wireOp",EDGE,"E58.MirrorCS")}),-1.0]])]});
            var Q31;
            Q31=makeQuery(id+"F2.imprint","IMPRINT",FACE,{"disambiguationData":[TD([[makeQuery(id+"F2.imprint","IMPRINT",EDGE,{"derivedFrom":sQuery(id+"F2.wireOp",EDGE,"E4.18.0.0")}),1.0]])]});
            var Q32;
            Q32=makeQuery(id+"F2.imprint","IMPRINT",FACE,{"disambiguationData":[TD([[makeQuery(id+"F2.imprint","IMPRINT",EDGE,{"derivedFrom":sQuery(id+"F2.wireOp",EDGE,"E22.MirrorCS")}),1.0]])]});
            var Q33;
            Q33=makeQuery(id+"F2.imprint","IMPRINT",FACE,{"disambiguationData":[TD([[makeQuery(id+"F2.imprint","IMPRINT",EDGE,{"derivedFrom":sQuery(id+"F2.wireOp",EDGE,"E56.MirrorCS")}),-1.0]])]});
            var Q34;
            Q34=makeQuery(id+"F2.imprint","IMPRINT",FACE,{"disambiguationData":[TD([[makeQuery(id+"F2.imprint","IMPRINT",EDGE,{"derivedFrom":sQuery(id+"F2.wireOp",EDGE,"E4.17.0.0")}),1.0]])]});
            var Q35;
            Q35=makeQuery(id+"F2.imprint","IMPRINT",FACE,{"disambiguationData":[TD([[makeQuery(id+"F2.imprint","IMPRINT",EDGE,{"derivedFrom":sQuery(id+"F2.wireOp",EDGE,"E8.MirrorCS")}),-1.0]])]});
            var Q36;
            Q36=makeQuery(id+"F2.imprint","IMPRINT",FACE,{"disambiguationData":[TD([[makeQuery(id+"F2.imprint","IMPRINT",EDGE,{"derivedFrom":sQuery(id+"F2.wireOp",EDGE,"E4.26.0.0")}),1.0]])]});
            var Q37;
            Q37=makeQuery(id+"F2.imprint","IMPRINT",FACE,{"disambiguationData":[TD([[makeQuery(id+"F2.imprint","IMPRINT",EDGE,{"derivedFrom":sQuery(id+"F2.wireOp",EDGE,"E87.MirrorCS")}),-1.0]])]});
            var Q38;
            Q38=makeQuery(id+"F2.imprint","IMPRINT",FACE,{"disambiguationData":[TD([[makeQuery(id+"F2.imprint","IMPRINT",EDGE,{"derivedFrom":sQuery(id+"F2.wireOp",EDGE,"E36.MirrorCS")}),-1.0]])]});
            var Q39;
            Q39=makeQuery(id+"F2.imprint","IMPRINT",FACE,{"disambiguationData":[TD([[makeQuery(id+"F2.imprint","IMPRINT",EDGE,{"derivedFrom":sQuery(id+"F2.wireOp",EDGE,"E4.16.0.0")}),1.0]])]});
            var Q40;
            Q40=makeQuery(id+"F2.imprint","IMPRINT",FACE,{"disambiguationData":[TD([[makeQuery(id+"F2.imprint","IMPRINT",EDGE,{"derivedFrom":sQuery(id+"F2.wireOp",EDGE,"E7.MirrorCS")}),1.0]])]});
            var Q41;
            Q41=makeQuery(id+"F2.imprint","IMPRINT",FACE,{"disambiguationData":[TD([[makeQuery(id+"F2.imprint","IMPRINT",EDGE,{"derivedFrom":sQuery(id+"F2.wireOp",EDGE,"E35.MirrorCS")}),-1.0]])]});
            var Q42;
            Q42=makeQuery(id+"F2.imprint","IMPRINT",FACE,{"disambiguationData":[TD([[makeQuery(id+"F2.imprint","IMPRINT",EDGE,{"derivedFrom":sQuery(id+"F2.wireOp",EDGE,"E4.25.0.0")}),1.0]])]});
            var Q43;
            Q43=makeQuery(id+"F2.imprint","IMPRINT",FACE,{"disambiguationData":[TD([[makeQuery(id+"F2.imprint","IMPRINT",EDGE,{"derivedFrom":sQuery(id+"F2.wireOp",EDGE,"E19.MirrorCS")}),1.0]])]});
            var Q44;
            Q44=makeQuery(id+"F2.imprint","IMPRINT",FACE,{"disambiguationData":[TD([[makeQuery(id+"F2.imprint","IMPRINT",EDGE,{"derivedFrom":sQuery(id+"F2.wireOp",EDGE,"E4.15.0.0")}),1.0]])]});
            var Q45;
            Q45=makeQuery(id+"F2.imprint","IMPRINT",FACE,{"disambiguationData":[TD([[makeQuery(id+"F2.imprint","IMPRINT",EDGE,{"derivedFrom":sQuery(id+"F2.wireOp",EDGE,"E86.MirrorCS")}),-1.0]])]});
            var Q46;
            Q46=makeQuery(id+"F2.imprint","IMPRINT",FACE,{"disambiguationData":[TD([[makeQuery(id+"F2.imprint","IMPRINT",EDGE,{"derivedFrom":sQuery(id+"F2.wireOp",EDGE,"E17.MirrorCS")}),-1.0]])]});
            var Q47;
            Q47=makeQuery(id+"F2.imprint","IMPRINT",FACE,{"disambiguationData":[TD([[makeQuery(id+"F2.imprint","IMPRINT",EDGE,{"derivedFrom":sQuery(id+"F2.wireOp",EDGE,"E85.MirrorCS")}),-1.0]])]});
            var Q48;
            Q48=makeQuery(id+"F2.imprint","IMPRINT",FACE,{"disambiguationData":[TD([[makeQuery(id+"F2.imprint","IMPRINT",EDGE,{"derivedFrom":sQuery(id+"F2.wireOp",EDGE,"E16.MirrorCS")}),-1.0]])]});
            var Q49;
            Q49=makeQuery(id+"F2.imprint","IMPRINT",FACE,{"disambiguationData":[TD([[makeQuery(id+"F2.imprint","IMPRINT",EDGE,{"derivedFrom":sQuery(id+"F2.wireOp",EDGE,"E84.MirrorCS")}),-1.0]])]});
            var Q50;
            Q50=makeQuery(id+"F2.imprint","IMPRINT",FACE,{"disambiguationData":[TD([[makeQuery(id+"F2.imprint","IMPRINT",EDGE,{"derivedFrom":sQuery(id+"F2.wireOp",EDGE,"E13.MirrorCS")}),-1.0]])]});
            var Q51;
            Q51=makeQuery(id+"F2.imprint","IMPRINT",FACE,{"disambiguationData":[TD([[makeQuery(id+"F2.imprint","IMPRINT",EDGE,{"derivedFrom":sQuery(id+"F2.wireOp",EDGE,"E4.21.0.0")}),1.0]])]});
            var Q52;
            Q52=makeQuery(id+"F2.imprint","IMPRINT",FACE,{"disambiguationData":[TD([[makeQuery(id+"F2.imprint","IMPRINT",EDGE,{"derivedFrom":sQuery(id+"F2.wireOp",EDGE,"E12.MirrorCS")}),-1.0]])]});
            var Q53;
            Q53=makeQuery(id+"F2.imprint","IMPRINT",FACE,{"disambiguationData":[TD([[makeQuery(id+"F2.imprint","IMPRINT",EDGE,{"derivedFrom":sQuery(id+"F2.wireOp",EDGE,"E61.MirrorCS")}),-1.0]])]});
            var Q54;
            Q54=makeQuery(id+"F2.imprint","IMPRINT",FACE,{"disambiguationData":[TD([[makeQuery(id+"F2.imprint","IMPRINT",EDGE,{"derivedFrom":sQuery(id+"F2.wireOp",EDGE,"E33.MirrorCS")}),-1.0]])]});
            var Q55;
            Q55=makeQuery(id+"F2.imprint","IMPRINT",FACE,{"disambiguationData":[TD([[makeQuery(id+"F2.imprint","IMPRINT",EDGE,{"derivedFrom":sQuery(id+"F2.wireOp",EDGE,"E4.29.0.0")}),1.0]])]});
            var Q56;
            Q56=makeQuery(id+"F2.imprint","IMPRINT",FACE,{"disambiguationData":[TD([[makeQuery(id+"F2.imprint","IMPRINT",EDGE,{"derivedFrom":sQuery(id+"F2.wireOp",EDGE,"E26.MirrorCS")}),-1.0]])]});
            var Q57;
            Q57=makeQuery(id+"F2.imprint","IMPRINT",FACE,{"disambiguationData":[TD([[makeQuery(id+"F2.imprint","IMPRINT",EDGE,{"derivedFrom":sQuery(id+"F2.wireOp",EDGE,"E4.28.0.0")}),1.0]])]});
            var Q58;
            Q58=makeQuery(id+"F2.imprint","IMPRINT",FACE,{"disambiguationData":[TD([[makeQuery(id+"F2.imprint","IMPRINT",EDGE,{"derivedFrom":sQuery(id+"F2.wireOp",EDGE,"E34.MirrorCS")}),-1.0]])]});
            var Q59;
            Q59=makeQuery(id+"F2.imprint","IMPRINT",FACE,{"disambiguationData":[TD([[makeQuery(id+"F2.imprint","IMPRINT",EDGE,{"derivedFrom":sQuery(id+"F2.wireOp",EDGE,"E89.MirrorCS")}),-1.0]])]});
            var Q60;
            Q60=makeQuery(id+"F2.imprint","IMPRINT",FACE,{"disambiguationData":[TD([[makeQuery(id+"F2.imprint","IMPRINT",EDGE,{"derivedFrom":sQuery(id+"F2.wireOp",EDGE,"E20.MirrorCS")}),1.0]])]});
            var Q61;
            Q61=makeQuery(id+"F1.opExtrude","CAP_FACE",FACE,{"disambiguationData":[OSD([sQuery(id+"F0.wireOp",EDGE,"E0.bottom"),sQuery(id+"F0.wireOp",EDGE,"E0.top"),sQuery(id+"F0.wireOp",EDGE,"E0.left"),sQuery(id+"F0.wireOp",EDGE,"E0.right")])],"isStart":true});
            extrude(context, id + "F3", {"entities" : qUnion([Q0, Q1, Q2, Q3, Q4, Q5, Q6, Q7, Q8, Q9, Q10, Q11, Q12, Q13, Q14, Q15, Q16, Q17, Q18, Q19, Q20, Q21, Q22, Q23, Q24, Q25, Q26, Q27, Q28, Q29, Q30, Q31, Q32, Q33, Q34, Q35, Q36, Q37, Q38, Q39, Q40, Q41, Q42, Q43, Q44, Q45, Q46, Q47, Q48, Q49, Q50, Q51, Q52, Q53, Q54, Q55, Q56, Q57, Q58, Q59, Q60]), "operationType" : NewBodyOperationType.REMOVE, "endBound" : BoundingType.UP_TO_SURFACE, "oppositeDirection" : true, "depth" : 25 * mm, "endBoundEntityFace" : qUnion([Q61]), "offsetDistance" : 25 * mm});
        }
    });
